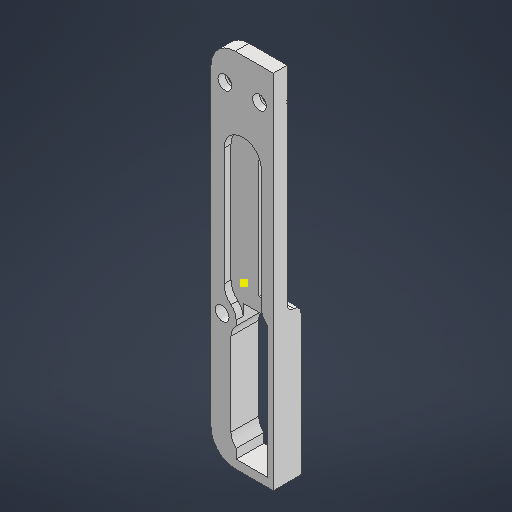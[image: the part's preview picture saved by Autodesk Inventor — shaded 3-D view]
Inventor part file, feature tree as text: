
AUTODESK INVENTOR PART (.ipt)
format: ipt  version: 2025 (Build 290162000, 162)  size: 305,664 bytes
history: native  units: mm
features: reference x12, sketch x10, extrude x7, other x5, fillet x2, chamfer x1
ambient origin geometry x8: Origin, YZ Plane, XZ Plane, XY Plane, X Axis, Y Axis, Z Axis, Center Point
bodies: 实体1 (feature_tree)
feature tree (37):
  sketch  "草图1"  dims[d0=4.0mm d1=0.0mm d2=4.0mm d3=0.0mm]
  extrude  "拉伸1"  Depth=4.0mm TaperAngle=0.0deg
  sketch  "草图3"  dims[d7=2.0mm d8=33.0mm d9=0.0mm]
  extrude  "拉伸2"  Depth=1.0mm
  extrude  "拉伸3"  Depth=33.0mm TaperAngle=0.0deg
  extrude  "拉伸4"  Depth=1.0mm
  fillet  "圆角1"  Radius=1.0mm
  extrude  "拉伸5"  Depth=1.0mm TaperAngle=0.0deg
  fillet  "圆角2"  Radius=2.0mm
  extrude  "拉伸6"  Depth=2.0mm
  sketch  "草图9"
  extrude  "拉伸7"  Depth=2.0mm
  chamfer  "倒角1"  Distance=9.5mm
  sketch  "草图2"  dims[d4=2.0mm d5=0.0mm d6=1.0mm]
  reference  "参考1"
  reference  "参考2"
  sketch  "草图4"  dims[d10=1.0mm d11=1.0mm d12=1.0mm d13=0.0mm]
  reference  "参考3"
  reference  "参考4"
  sketch  "草图5"  dims[d14=2.0mm d15=1.0mm d16=0.0mm d17=2.0mm]
  reference  "参考5"
  sketch  "草图6"  dims[d18=2.0mm d19=2.0mm]
  reference  "参考6"
  sketch  "草图7"  dims[d20=2.0mm d21=2.0mm d22=9.5mm d23=0.0mm]
  reference  "参考7"
  reference  "参考8"
  reference  "参考9"
  reference  "参考10"
  reference  "参考11"
  reference  "参考12"
  sketch  "草图8"  dims[d24=1.0mm d25=2.0mm d26=45.0deg]
  sketch  "草图10"
  parser-record x1  (decoder bookkeeping rows leaked as tree rows — omitted from the tree; the rows remain in map.json)
  other  "dlc.iam"
  other  "指纹dlc:1"
  other  "指纹识别:1"
  other  "音量接口:1"
note: 1 file-system path scrubbed to <path> (originals preserved in map.json)
